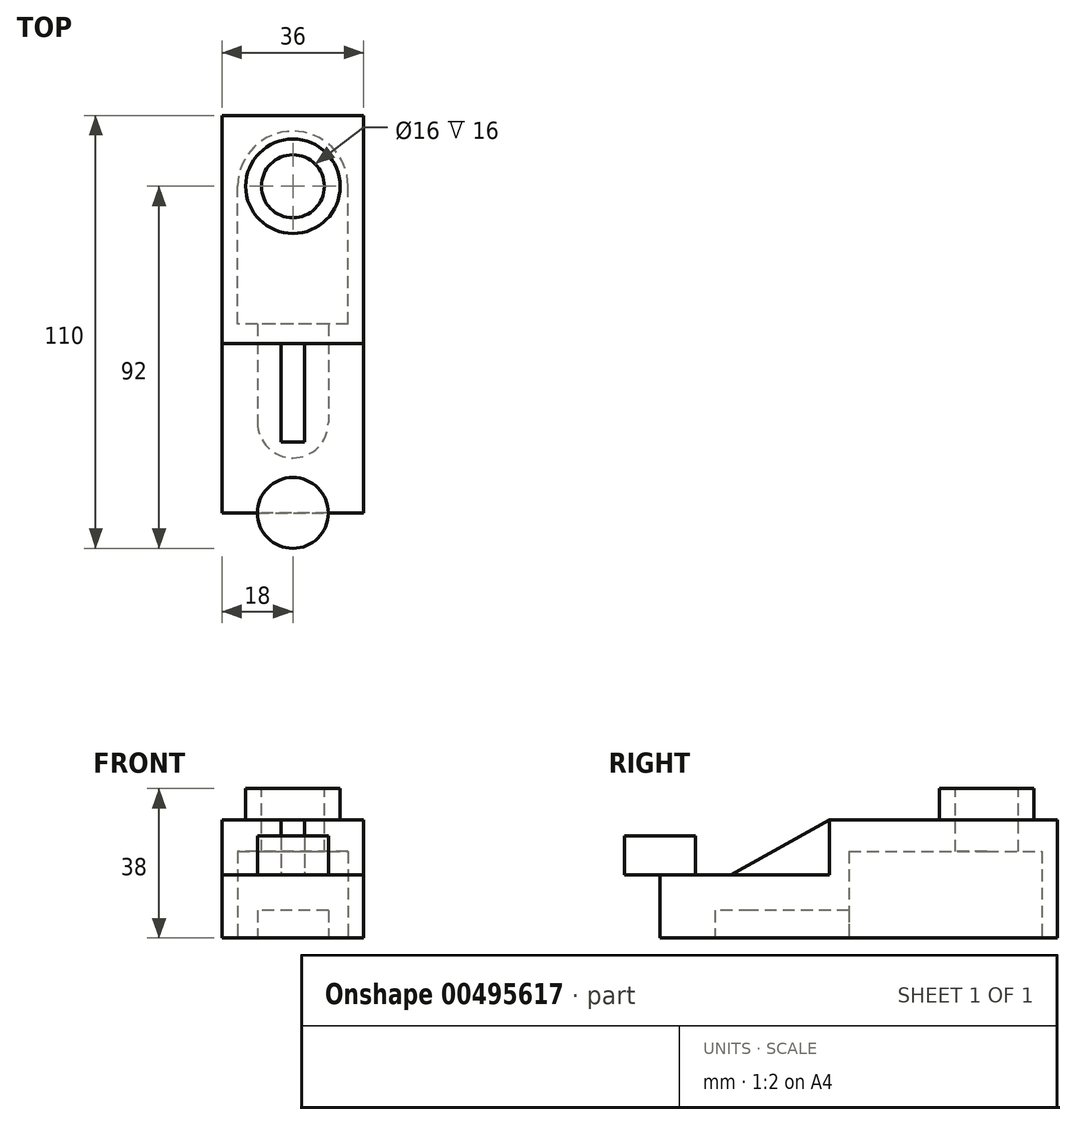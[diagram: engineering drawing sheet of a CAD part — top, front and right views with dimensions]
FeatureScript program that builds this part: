
annotation { "Feature Type Name" : "Feature", "Feature Type Description" : "" }
export const myFeature = defineFeature(function(context is Context, id is Id, definition is map)
    precondition{}
    {
        {
            var Q0;
            Q0=qCreatedBy(makeId("Right.planeOp"),FACE);
            var sketch = newSketch(context, id + "F0", { "sketchPlane" : qUnion([Q0])});
            skLineSegment(sketch, "E0.bottom", {"start": v(50.5, 15) * mm, "end": v(-50.5, 15) * mm});
            skLineSegment(sketch, "E0.top", {"start": v(50.5, -15) * mm, "end": v(-50.5, -15) * mm});
            skLineSegment(sketch, "E0.left", {"start": v(50.5, 15) * mm, "end": v(50.5, -15) * mm});
            skLineSegment(sketch, "E0.right", {"start": v(-50.5, 15) * mm, "end": v(-50.5, -15) * mm});
            skPoint(sketch, "E0.middle", {"position": v(0, 0) * mm});
            skSolve(sketch);
        }
        {
            var Q0;
            Q0=makeQuery(id+"F0.imprint","IMPRINT",FACE,{"disambiguationData":[TD([[makeQuery(id+"F0.imprint","IMPRINT",EDGE,{"derivedFrom":sQuery(id+"F0.wireOp",EDGE,"E0.bottom")}),1.0]])]});
            extrude(context, id + "F1", {"entities" : qUnion([Q0]), "endBound" : BoundingType.SYMMETRIC, "depth" : 36 * mm, "offsetDistance" : 25 * mm});
        }
        {
            var Q0;
            Q0=makeQuery(id+"F1.opExtrude","SWEPT_FACE",FACE,{"disambiguationData":[OSD([sQuery(id+"F0.wireOp",EDGE,"E0.bottom")])]});
            var sketch = newSketch(context, id + "F2", { "sketchPlane" : qUnion([Q0])});
            skCircle(sketch, "E1", {"center": v(0, 32.5) * mm, "radius": 12 * mm});
            skPoint(sketch, "E1.centerSnap0", {"position": v(0, 50.5) * mm});
            skSolve(sketch);
        }
        {
            var Q0;
            Q0 = qSketchRegion(id + "F2", true);
            extrude(context, id + "F3", {"entities" : qUnion([Q0]), "operationType" : NewBodyOperationType.ADD, "depth" : 8 * mm, "offsetDistance" : 25 * mm});
        }
        {
            var Q0;
            Q0=makeQuery(id+"F3.opExtrude","CAP_FACE",FACE,{"disambiguationData":[OSD([sQuery(id+"F2.wireOp",EDGE,"E1")])],"isStart":false});
            var sketch = newSketch(context, id + "F4", { "sketchPlane" : qUnion([Q0])});
            skCircle(sketch, "E2", {"center": v(0, 32.5) * mm, "radius": 8 * mm});
            skSolve(sketch);
        }
        {
            var Q0;
            Q0=makeQuery(id+"F4.imprint","IMPRINT",FACE,{"disambiguationData":[TD([[makeQuery(id+"F4.imprint","IMPRINT",EDGE,{"derivedFrom":sQuery(id+"F4.wireOp",EDGE,"E2")}),1.0]])]});
            extrude(context, id + "F5", {"entities" : qUnion([Q0]), "operationType" : NewBodyOperationType.REMOVE, "endBound" : BoundingType.THROUGH_ALL, "oppositeDirection" : true, "depth" : 25 * mm, "offsetDistance" : 25 * mm});
        }
        {
            var Q0;
            Q0=makeQuery(id+"F1.opExtrude","CAP_FACE",FACE,{"disambiguationData":[OSD([sQuery(id+"F0.wireOp",EDGE,"E0.bottom"),sQuery(id+"F0.wireOp",EDGE,"E0.top"),sQuery(id+"F0.wireOp",EDGE,"E0.left"),sQuery(id+"F0.wireOp",EDGE,"E0.right")])],"isStart":false});
            var sketch = newSketch(context, id + "F6", { "sketchPlane" : qUnion([Q0])});
            skLineSegment(sketch, "E3.bottom", {"start": v(-50.5, 15) * mm, "end": v(-7.5, 15) * mm});
            skLineSegment(sketch, "E3.top", {"start": v(-50.5, 1) * mm, "end": v(-7.5, 1) * mm});
            skLineSegment(sketch, "E3.left", {"start": v(-50.5, 15) * mm, "end": v(-50.5, 1) * mm});
            skLineSegment(sketch, "E3.right", {"start": v(-7.5, 15) * mm, "end": v(-7.5, 1) * mm});
            skSolve(sketch);
        }
        {
            var Q0;
            Q0 = qSketchRegion(id + "F6", true);
            extrude(context, id + "F7", {"entities" : qUnion([Q0]), "operationType" : NewBodyOperationType.REMOVE, "endBound" : BoundingType.THROUGH_ALL, "oppositeDirection" : true, "depth" : 25 * mm, "offsetDistance" : 25 * mm});
        }
        {
            var Q0;
            Q0=makeQuery(id+"F7.boolean.opBoolean","COPY",FACE,{"derivedFrom":makeQuery(id+"F7.opExtrude","SWEPT_FACE",FACE,{"disambiguationData":[OSD([sQuery(id+"F6.wireOp",EDGE,"E3.top")])]})});
            var sketch = newSketch(context, id + "F8", { "sketchPlane" : qUnion([Q0])});
            skCircle(sketch, "E4", {"center": v(0, -50.5) * mm, "radius": 9 * mm});
            skSolve(sketch);
        }
        {
            var Q0;
            {var subQ0=sQuery(id+"F8.wireOp",EDGE,"E4");var subQ1=makeQuery(id+"F7.boolean.opBoolean","COPY",EDGE,{"derivedFrom":makeQuery(id+"F7.opExtrude","SWEPT_EDGE",EDGE,{"disambiguationData":[OSD([sQuery(id+"F0.wireOp",EDGE,"E0.right"),sQuery(id+"F6.wireOp",EDGE,"E3.top"),sQuery(id+"F6.wireOp",EDGE,"E3.left")])]})});var subQ2=makeQuery(id+"F8.imprint","INTERSECT",VERTEX,{"disambiguationData":[OD(0.0)],"derivedFrom":[subQ1,subQ0]});Q0=makeQuery(id+"F8.imprint","IMPRINT",FACE,{"disambiguationData":[TD([[makeQuery(id+"F8.imprint","IMPRINT",EDGE,{"disambiguationData":[TD([[subQ2,1.0]])],"derivedFrom":subQ0}),1.0]])]});}
            extrude(context, id + "F9", {"entities" : qUnion([Q0]), "operationType" : NewBodyOperationType.ADD, "oppositeDirection" : true, "depth" : 16 * mm, "offsetDistance" : 25 * mm});
        }
        {
            var Q0;
            Q0 = qSketchRegion(id + "F8", true);
            extrude(context, id + "F10", {"entities" : qUnion([Q0]), "operationType" : NewBodyOperationType.ADD, "depth" : 10 * mm, "offsetDistance" : 25 * mm});
        }
        {
            var Q0;
            Q0=qCreatedBy(makeId("Right.planeOp"),FACE);
            var sketch = newSketch(context, id + "F11", { "sketchPlane" : qUnion([Q0])});
            skLineSegment(sketch, "E5", {"start": v(-7.5, 15) * mm, "end": v(-32.5, 1) * mm});
            skLineSegment(sketch, "E6", {"start": v(-7.5, 15) * mm, "end": v(-7.5, 1) * mm});
            skLineSegment(sketch, "E7", {"start": v(-7.5, 1) * mm, "end": v(-32.5, 1) * mm});
            skSolve(sketch);
        }
        {
            var Q0;
            Q0 = qSketchRegion(id + "F11", true);
            extrude(context, id + "F12", {"entities" : qUnion([Q0]), "operationType" : NewBodyOperationType.ADD, "endBound" : BoundingType.SYMMETRIC, "depth" : 6 * mm, "offsetDistance" : 25 * mm});
        }
        {
            var Q0;
            Q0=makeQuery(id+"F9.boolean.opBoolean","MERGE",FACE,{"derivedFrom":[makeQuery(id+"F1.opExtrude","SWEPT_FACE",FACE,{"disambiguationData":[OSD([sQuery(id+"F0.wireOp",EDGE,"E0.top")])]}),makeQuery(id+"F9.opExtrude","CAP_FACE",FACE,{"disambiguationData":[OSD([sQuery(id+"F0.wireOp",EDGE,"E0.right"),sQuery(id+"F6.wireOp",EDGE,"E3.top"),sQuery(id+"F6.wireOp",EDGE,"E3.left"),sQuery(id+"F8.wireOp",EDGE,"E4")])],"isStart":false})]});
            var sketch = newSketch(context, id + "F13", { "sketchPlane" : qUnion([Q0])});
            skArc(sketch, "E8", {"start": v(-14, -32.5) * mm, "mid": v(0, -46.5) * mm, "end": v(14, -32.5) * mm});
            skLineSegment(sketch, "E9.bottom", {"start": v(14, 2.5) * mm, "end": v(-14, 2.5) * mm});
            skLineSegment(sketch, "E9.left", {"start": v(14, 2.5) * mm, "end": v(14, -32.5) * mm});
            skLineSegment(sketch, "E9.right", {"start": v(-14, 2.5) * mm, "end": v(-14, -32.5) * mm});
            skSolve(sketch);
        }
        {
            var Q0;
            Q0=makeQuery(id+"F13.imprint","IMPRINT",FACE,{"disambiguationData":[TD([[makeQuery(id+"F13.imprint","IMPRINT",EDGE,{"derivedFrom":sQuery(id+"F13.wireOp",EDGE,"E8")}),1.0]])]});
            extrude(context, id + "F14", {"entities" : qUnion([Q0]), "operationType" : NewBodyOperationType.REMOVE, "oppositeDirection" : true, "depth" : 22 * mm, "offsetDistance" : 25 * mm});
        }
        {
            var Q0;
            Q0=makeQuery(id+"F9.boolean.opBoolean","MERGE",FACE,{"derivedFrom":[makeQuery(id+"F1.opExtrude","SWEPT_FACE",FACE,{"disambiguationData":[OSD([sQuery(id+"F0.wireOp",EDGE,"E0.top")])]}),makeQuery(id+"F9.opExtrude","CAP_FACE",FACE,{"disambiguationData":[OSD([sQuery(id+"F0.wireOp",EDGE,"E0.right"),sQuery(id+"F6.wireOp",EDGE,"E3.top"),sQuery(id+"F6.wireOp",EDGE,"E3.left"),sQuery(id+"F8.wireOp",EDGE,"E4")])],"isStart":false})]});
            var sketch = newSketch(context, id + "F15", { "sketchPlane" : qUnion([Q0])});
            skArc(sketch, "E10", {"start": v(9, 27.5) * mm, "mid": v(0, 36.5) * mm, "end": v(-9, 27.5) * mm});
            skLineSegment(sketch, "E11.bottom", {"start": v(9, 2.5) * mm, "end": v(-9, 2.5) * mm});
            skLineSegment(sketch, "E11.left", {"start": v(9, 2.5) * mm, "end": v(9, 27.5) * mm});
            skLineSegment(sketch, "E11.right", {"start": v(-9, 2.5) * mm, "end": v(-9, 27.5) * mm});
            skSolve(sketch);
        }
        {
            var Q0;
            Q0 = qSketchRegion(id + "F15", true);
            extrude(context, id + "F16", {"entities" : qUnion([Q0]), "operationType" : NewBodyOperationType.REMOVE, "oppositeDirection" : true, "depth" : 7 * mm, "offsetDistance" : 25 * mm});
        }
    });
